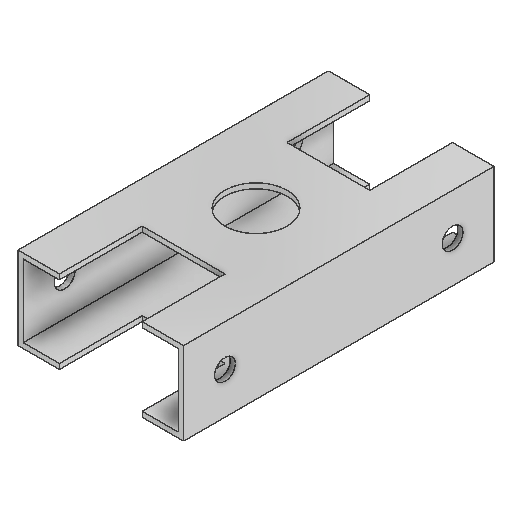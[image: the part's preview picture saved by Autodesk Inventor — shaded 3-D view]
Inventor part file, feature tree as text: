
AUTODESK INVENTOR PART (.ipt)
format: ipt  version: 2025.2 (Build 292293000, 293)  size: 171,008 bytes
history: native  units: in
note: dims shown in document units (in); Inventor stores cm internally (conversion verified against a paired STEP export)
features: extrude x3, sketch x3
ambient origin geometry x8: Origin, YZ Plane, XZ Plane, XY Plane, X Axis, Y Axis, Z Axis, Center Point
bodies: Solid1 (feature_tree)
feature tree (6):
  extrude  "Extrusion1"  Depth=1.0in
  extrude  "Extrusion2"  Depth=0.0625in
  extrude  "Extrusion3"  Depth=0.0625in
  sketch  "Sketch1"  dims[d0=2.0in d1=1.0in]
  sketch  "Sketch2"  dims[d2=0.0625in d3=0.0625in]
  sketch  "Sketch3"  dims[d4=0.0625in d5=0.0625in d6=3.75in d7=0.0in d8=0.75in d9=1.0in d10=1.875in d11=4.6in d12=0.0in d13=1.0in d14=1.0in d15=1.0in d16=1.0in d17=0.25in d18=0.5in d19=0.5in d20=0.25in d21=0.5in d22=0.5in d23=0.0in d24=0.0in d25=3.75in]
